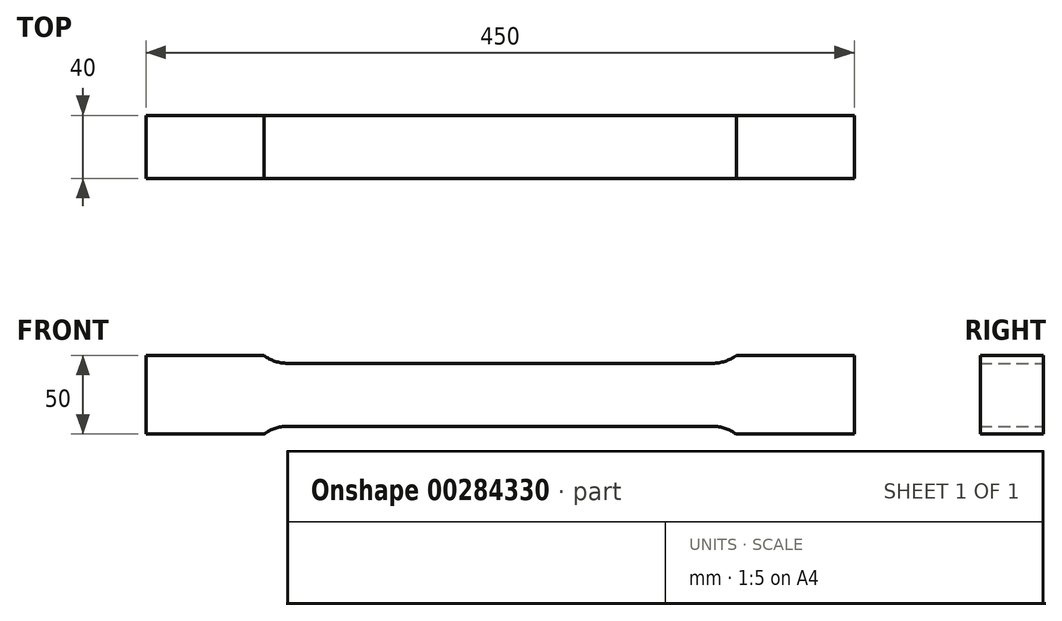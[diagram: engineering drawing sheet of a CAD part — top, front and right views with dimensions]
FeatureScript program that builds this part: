
annotation { "Feature Type Name" : "Feature", "Feature Type Description" : "" }
export const myFeature = defineFeature(function(context is Context, id is Id, definition is map)
    precondition{}
    {
        {
            var Q0;
            Q0=qCreatedBy(makeId("Front.planeOp"),FACE);
            var sketch = newSketch(context, id + "F0", { "sketchPlane" : qUnion([Q0])});
            skLineSegment(sketch, "E0", {"start": v(0, 20) * mm, "end": v(135, 20) * mm});
            skArc(sketch, "E1", {"start": v(135, 20) * mm, "mid": v(142.9, 21.28) * mm, "end": v(150, 25) * mm});
            skLineSegment(sketch, "E2", {"start": v(150, 25) * mm, "end": v(225, 25) * mm});
            skLineSegment(sketch, "E3", {"start": v(225, 25) * mm, "end": v(225, 0) * mm});
            skLineSegment(sketch, "E4.MirrorCS", {"start": v(0, -20) * mm, "end": v(135, -20) * mm});
            skLineSegment(sketch, "E5.MirrorCS", {"start": v(225, -25) * mm, "end": v(225, 0) * mm});
            skLineSegment(sketch, "E6.MirrorCS", {"start": v(150, -25) * mm, "end": v(225, -25) * mm});
            skArc(sketch, "E7.MirrorCS", {"start": v(135, -20) * mm, "mid": v(142.9, -21.28) * mm, "end": v(150, -25) * mm});
            skArc(sketch, "E8.MirrorCS", {"start": v(-135, 20) * mm, "mid": v(-142.9, 21.28) * mm, "end": v(-150, 25) * mm});
            skArc(sketch, "E9.MirrorCS", {"start": v(-135, -20) * mm, "mid": v(-142.9, -21.28) * mm, "end": v(-150, -25) * mm});
            skLineSegment(sketch, "E10.MirrorCS", {"start": v(-150, -25) * mm, "end": v(-225, -25) * mm});
            skLineSegment(sketch, "E11.MirrorCS", {"start": v(-150, 25) * mm, "end": v(-225, 25) * mm});
            skLineSegment(sketch, "E12.MirrorCS", {"start": v(-225, -25) * mm, "end": v(-225, 0) * mm});
            skLineSegment(sketch, "E13.MirrorCS", {"start": v(0, -20) * mm, "end": v(-135, -20) * mm});
            skLineSegment(sketch, "E14.MirrorCS", {"start": v(-225, 25) * mm, "end": v(-225, 0) * mm});
            skLineSegment(sketch, "E15.MirrorCS", {"start": v(0, 20) * mm, "end": v(-135, 20) * mm});
            skSolve(sketch);
        }
        {
            var Q0;
            Q0 = qSketchRegion(id + "F0", true);
            extrude(context, id + "F1", {"entities" : qUnion([Q0]), "endBound" : BoundingType.SYMMETRIC, "depth" : 40 * mm});
        }
    });
